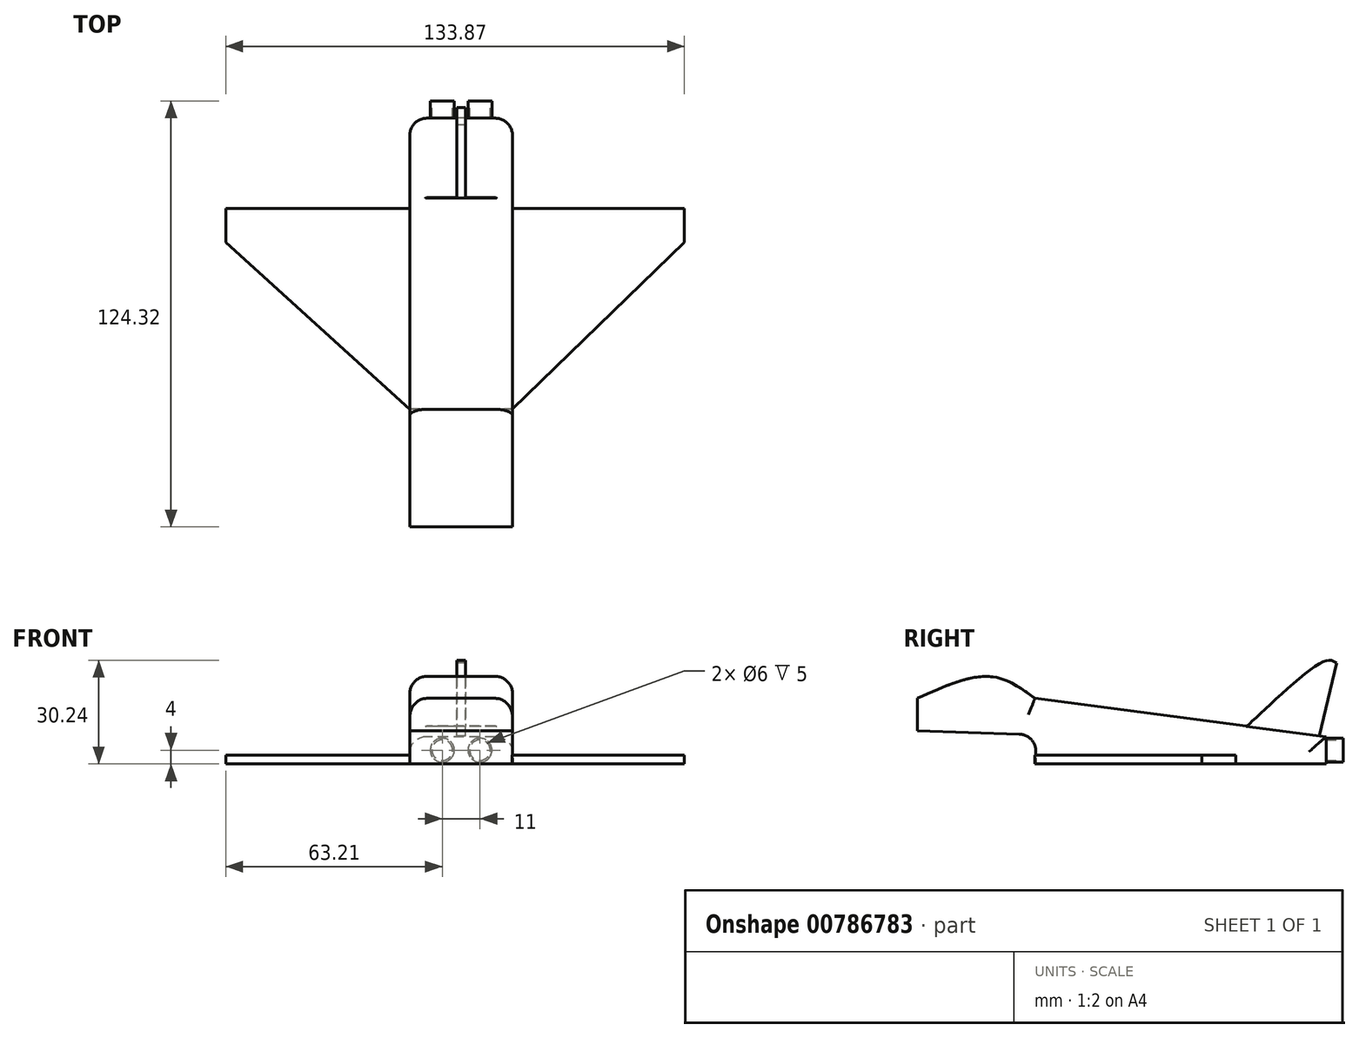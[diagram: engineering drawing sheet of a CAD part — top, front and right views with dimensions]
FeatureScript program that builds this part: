
annotation { "Feature Type Name" : "Feature", "Feature Type Description" : "" }
export const myFeature = defineFeature(function(context is Context, id is Id, definition is map)
    precondition{}
    {
        {
            var Q0;
            Q0=qCreatedBy(makeId("Right.planeOp"),FACE);
            var sketch = newSketch(context, id + "F0", { "sketchPlane" : qUnion([Q0])});
            skLineSegment(sketch, "E0", {"start": v(85, 0) * mm, "end": v(85, 7.93) * mm});
            skLineSegment(sketch, "E1", {"start": v(85, 7.93) * mm, "end": v(0, 19.15) * mm});
            skFitSpline(sketch, "E2", {"points": [v(0, 19.15) * mm, v(-13.01, 25.5) * mm, v(-34.32, 19.15) * mm], "startDerivative": vector(-27, 19.9) * mm, "endDerivative": vector(-40.45, -18.58) * mm});
            skLineSegment(sketch, "E3", {"start": v(0.68, 8.52) * mm, "end": v(0, 0) * mm});
            skLineSegment(sketch, "E4", {"start": v(0, 0) * mm, "end": v(85, 0) * mm});
            skLineSegment(sketch, "E5", {"start": v(-34.32, 9.63) * mm, "end": v(0.68, 8.52) * mm});
            skLineSegment(sketch, "E6", {"start": v(-34.32, 19.15) * mm, "end": v(-34.32, 9.63) * mm});
            skLineSegment(sketch, "E7", {"start": v(82.97, 8.2) * mm, "end": v(88.12, 29.51) * mm});
            skFitSpline(sketch, "E8", {"points": [v(88.12, 29.51) * mm, v(83.5, 29.51) * mm, v(61.75, 11) * mm, v(61.67, 11.01) * mm], "startDerivative": vector(-11.75, 6.89) * mm, "endDerivative": vector(-1.17, 1.44) * mm});
            skSolve(sketch);
        }
        {
            var Q0;
            Q0=makeQuery(id+"F0.imprint","IMPRINT",FACE,{"disambiguationData":[TD([[makeQuery(id+"F0.imprint","IMPRINT",EDGE,{"derivedFrom":sQuery(id+"F0.wireOp",EDGE,"E0")}),1.0]])]});
            extrude(context, id + "F1", {"entities" : qUnion([Q0]), "endBound" : BoundingType.SYMMETRIC, "depth" : 30 * mm, "offsetDistance" : 25 * mm});
        }
        {
            var Q0;
            {var subQ0=sQuery(id+"F0.wireOp",EDGE,"E7");Q0=makeQuery(id+"F0.imprint","IMPRINT",FACE,{"disambiguationData":[TD([[makeQuery(id+"F0.imprint","IMPRINT",EDGE,{"derivedFrom":subQ0}),1.0]])]});}
            extrude(context, id + "F2", {"entities" : qUnion([Q0]), "operationType" : NewBodyOperationType.ADD, "endBound" : BoundingType.SYMMETRIC, "depth" : 2.5 * mm, "offsetDistance" : 25 * mm});
        }
        {
            var Q0;
            Q0=makeQuery(id+"F1.opExtrude","CAP_EDGE",EDGE,{"disambiguationData":[OSD([sQuery(id+"F0.wireOp",EDGE,"E0")])],"isStart":false});
            var Q1;
            Q1=makeQuery(id+"F1.opExtrude","CAP_EDGE",EDGE,{"disambiguationData":[OSD([sQuery(id+"F0.wireOp",EDGE,"E0")])],"isStart":true});
            fillet(context, id + "F3", {"entities" : qUnion([Q0, Q1]), "radius" : 5 * mm, "tangentPropagation" : true, "allowEdgeOverflow" : false});
        }
        {
            var Q0;
            Q0=makeQuery(id+"F1.opExtrude","SWEPT_FACE",FACE,{"disambiguationData":[OSD([sQuery(id+"F0.wireOp",EDGE,"E0")])]});
            var sketch = newSketch(context, id + "F4", { "sketchPlane" : qUnion([Q0])});
            skCircle(sketch, "E9", {"center": v(-5.5, 4) * mm, "radius": 3.5 * mm});
            skCircle(sketch, "E10", {"center": v(5.5, 4) * mm, "radius": 3.5 * mm});
            skSolve(sketch);
        }
        {
            var Q0;
            Q0=makeQuery(id+"F4.imprint","IMPRINT",FACE,{"disambiguationData":[TD([[makeQuery(id+"F4.imprint","IMPRINT",EDGE,{"derivedFrom":sQuery(id+"F4.wireOp",EDGE,"E9")}),1.0]])]});
            var Q1;
            Q1=makeQuery(id+"F4.imprint","IMPRINT",FACE,{"disambiguationData":[TD([[makeQuery(id+"F4.imprint","IMPRINT",EDGE,{"derivedFrom":sQuery(id+"F4.wireOp",EDGE,"E10")}),1.0]])]});
            extrude(context, id + "F5", {"entities" : qUnion([Q0, Q1]), "operationType" : NewBodyOperationType.ADD, "endBound" : BoundingType.SYMMETRIC, "depth" : 10 * mm, "offsetDistance" : 25 * mm});
        }
        {
            var Q0;
            Q0=makeQuery(id+"F5.opExtrude","CAP_FACE",FACE,{"disambiguationData":[OSD([sQuery(id+"F4.wireOp",EDGE,"E9")])],"isStart":false});
            var sketch = newSketch(context, id + "F6", { "sketchPlane" : qUnion([Q0])});
            skCircle(sketch, "E11", {"center": v(-5.5, 4) * mm, "radius": 3 * mm});
            skCircle(sketch, "E12", {"center": v(5.5, 4) * mm, "radius": 3 * mm});
            skSolve(sketch);
        }
        {
            var Q0;
            Q0=makeQuery(id+"F6.imprint","IMPRINT",FACE,{"disambiguationData":[TD([[makeQuery(id+"F6.imprint","IMPRINT",EDGE,{"derivedFrom":sQuery(id+"F6.wireOp",EDGE,"E11")}),1.0]])]});
            var Q1;
            Q1=makeQuery(id+"F6.imprint","IMPRINT",FACE,{"disambiguationData":[TD([[makeQuery(id+"F6.imprint","IMPRINT",EDGE,{"derivedFrom":sQuery(id+"F6.wireOp",EDGE,"E12")}),1.0]])]});
            extrude(context, id + "F7", {"entities" : qUnion([Q0, Q1]), "operationType" : NewBodyOperationType.REMOVE, "endBound" : BoundingType.SYMMETRIC, "oppositeDirection" : true, "depth" : 10 * mm, "offsetDistance" : 25 * mm});
        }
        {
            var Q0;
            Q0=qCreatedBy(makeId("Top.planeOp"),FACE);
            var sketch = newSketch(context, id + "F8", { "sketchPlane" : qUnion([Q0])});
            skLineSegment(sketch, "E13", {"start": v(14.87, 0) * mm, "end": v(65.16, 48.68) * mm});
            skLineSegment(sketch, "E14", {"start": v(65.16, 48.68) * mm, "end": v(65.16, 58.68) * mm});
            skLineSegment(sketch, "E15", {"start": v(65.16, 58.68) * mm, "end": v(14.16, 58.68) * mm});
            skLineSegment(sketch, "E16", {"start": v(14.16, 58.68) * mm, "end": v(14.87, 0) * mm});
            skLineSegment(sketch, "E17", {"start": v(-14.2, 58.68) * mm, "end": v(-68.7, 58.68) * mm});
            skLineSegment(sketch, "E18", {"start": v(-68.7, 58.68) * mm, "end": v(-68.7, 48.68) * mm});
            skLineSegment(sketch, "E19", {"start": v(-68.7, 48.68) * mm, "end": v(-14.99, 0) * mm});
            skLineSegment(sketch, "E20", {"start": v(-14.99, 0) * mm, "end": v(-14.2, 58.68) * mm});
            skSolve(sketch);
        }
        {
            var Q0;
            Q0=makeQuery(id+"F8.imprint","IMPRINT",FACE,{"disambiguationData":[TD([[makeQuery(id+"F8.imprint","IMPRINT",EDGE,{"derivedFrom":sQuery(id+"F8.wireOp",EDGE,"E17")}),1.0]])]});
            var Q1;
            Q1=makeQuery(id+"F8.imprint","IMPRINT",FACE,{"disambiguationData":[TD([[makeQuery(id+"F8.imprint","IMPRINT",EDGE,{"derivedFrom":sQuery(id+"F8.wireOp",EDGE,"E13")}),1.0]])]});
            extrude(context, id + "F9", {"entities" : qUnion([Q0, Q1]), "operationType" : NewBodyOperationType.ADD, "depth" : 2.5 * mm, "offsetDistance" : 25 * mm});
        }
        {
            var Q0;
            {var subQ0=sQuery(id+"F0.wireOp",EDGE,"E1");Q0=makeQuery(id+"F1.opExtrude","CAP_EDGE",EDGE,{"disambiguationData":[OSD([subQ0]),TDD([makeQuery(id+"F0.imprint","IMPRINT",EDGE,{"disambiguationData":[TD([[makeQuery(id+"F0.imprint","INTERSECT",VERTEX,{"derivedFrom":[subQ0,sQuery(id+"F0.wireOp",EDGE,"E2")]}),1.0]])],"derivedFrom":subQ0})])],"isStart":false});}
            var Q1;
            Q1=makeQuery(id+"F1.opExtrude","CAP_EDGE",EDGE,{"disambiguationData":[OSD([sQuery(id+"F0.wireOp",EDGE,"E2")])],"isStart":false});
            var Q2;
            Q2=makeQuery(id+"F1.opExtrude","CAP_EDGE",EDGE,{"disambiguationData":[OSD([sQuery(id+"F0.wireOp",EDGE,"E2")])],"isStart":true});
            var Q3;
            {var subQ0=sQuery(id+"F0.wireOp",EDGE,"E1");Q3=makeQuery(id+"F1.opExtrude","CAP_EDGE",EDGE,{"disambiguationData":[OSD([subQ0]),TDD([makeQuery(id+"F0.imprint","IMPRINT",EDGE,{"disambiguationData":[TD([[makeQuery(id+"F0.imprint","INTERSECT",VERTEX,{"derivedFrom":[subQ0,sQuery(id+"F0.wireOp",EDGE,"E2")]}),1.0]])],"derivedFrom":subQ0})])],"isStart":true});}
            fillet(context, id + "F10", {"entities" : qUnion([Q0, Q1, Q2, Q3]), "radius" : 5 * mm, "tangentPropagation" : true, "allowEdgeOverflow" : false});
        }
        {
            var Q0;
            Q0=makeQuery(id+"F1.opExtrude","SWEPT_EDGE",EDGE,{"disambiguationData":[OSD([sQuery(id+"F0.wireOp",EDGE,"E3"),sQuery(id+"F0.wireOp",EDGE,"E5")])]});
            fillet(context, id + "F11", {"entities" : qUnion([Q0]), "radius" : 5 * mm, "tangentPropagation" : true, "allowEdgeOverflow" : false});
        }
    });
